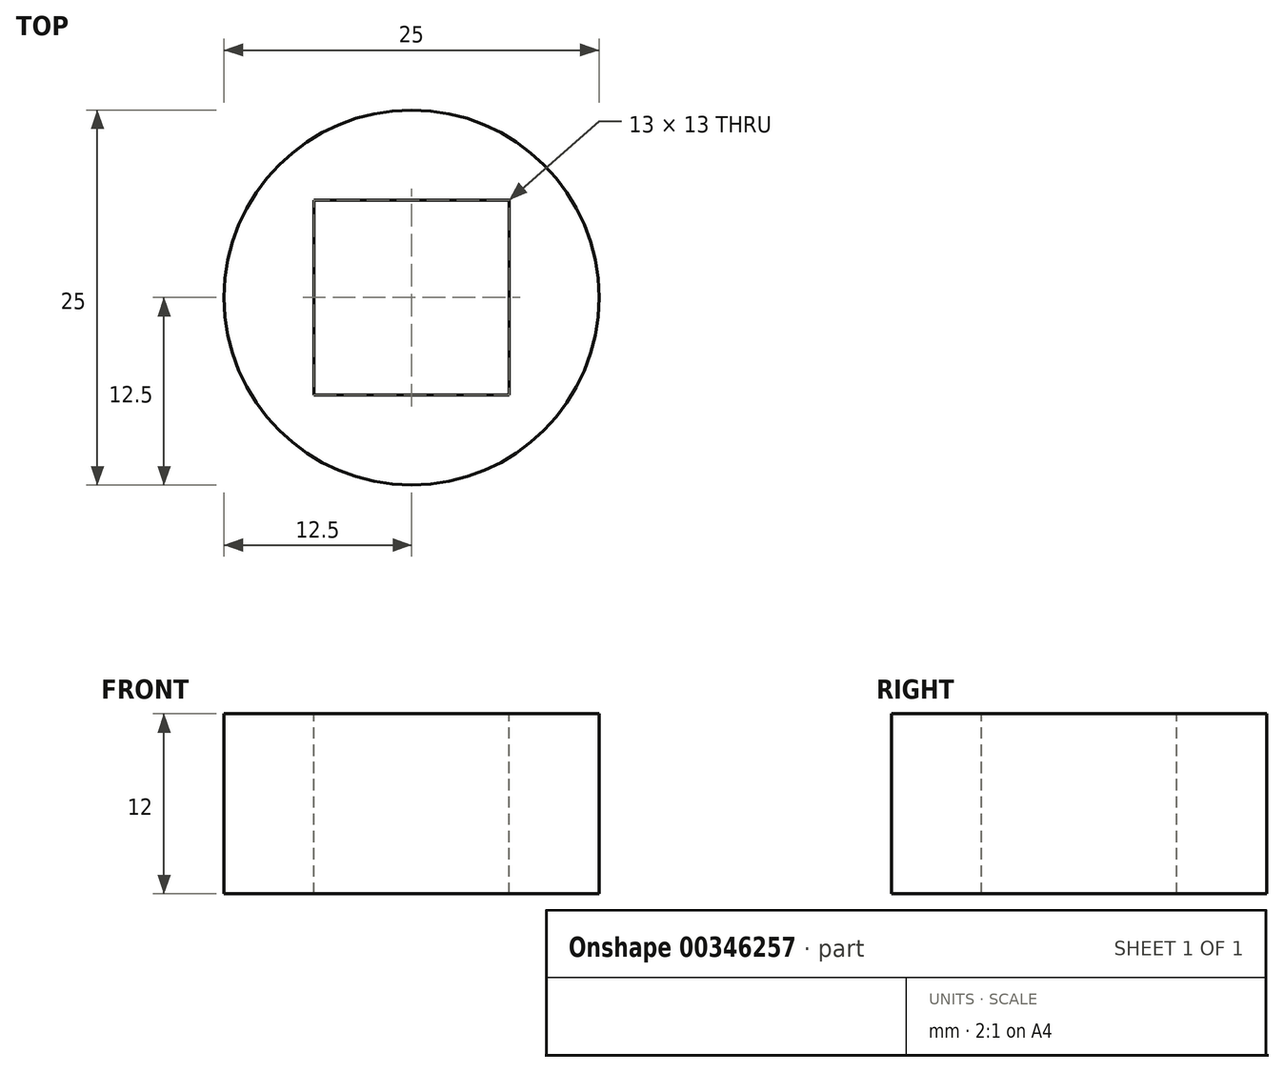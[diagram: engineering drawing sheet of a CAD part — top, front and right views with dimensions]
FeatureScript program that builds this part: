
annotation { "Feature Type Name" : "Feature", "Feature Type Description" : "" }
export const myFeature = defineFeature(function(context is Context, id is Id, definition is map)
    precondition{}
    {
        {
            var Q0;
            Q0=qCreatedBy(makeId("Top.planeOp"),FACE);
            var sketch = newSketch(context, id + "F0", { "sketchPlane" : qUnion([Q0])});
            skCircle(sketch, "E0", {"center": v(0, 0) * mm, "radius": 12.5 * mm});
            skSolve(sketch);
        }
        {
            var Q0;
            Q0 = qSketchRegion(id + "F0", true);
            extrude(context, id + "F1", {"entities" : qUnion([Q0]), "depth" : 12 * mm});
        }
        {
            var Q0;
            Q0=makeQuery(id+"F1.opExtrude","CAP_FACE",FACE,{"disambiguationData":[OSD([sQuery(id+"F0.wireOp",EDGE,"E0")])],"isStart":false});
            var sketch = newSketch(context, id + "F2", { "sketchPlane" : qUnion([Q0])});
            skLineSegment(sketch, "E1", {"start": v(6.5, 6.5) * mm, "end": v(-6.5, 6.5) * mm});
            skLineSegment(sketch, "E2", {"start": v(-6.5, 6.5) * mm, "end": v(-6.5, -6.5) * mm});
            skLineSegment(sketch, "E3", {"start": v(-6.5, -6.5) * mm, "end": v(6.5, -6.5) * mm});
            skLineSegment(sketch, "E4", {"start": v(6.5, -6.5) * mm, "end": v(6.5, 6.5) * mm});
            skSolve(sketch);
        }
        {
            var Q0;
            Q0 = qSketchRegion(id + "F2", true);
            extrude(context, id + "F3", {"entities" : qUnion([Q0]), "operationType" : NewBodyOperationType.REMOVE, "oppositeDirection" : true, "depth" : 25 * mm});
        }
    });
